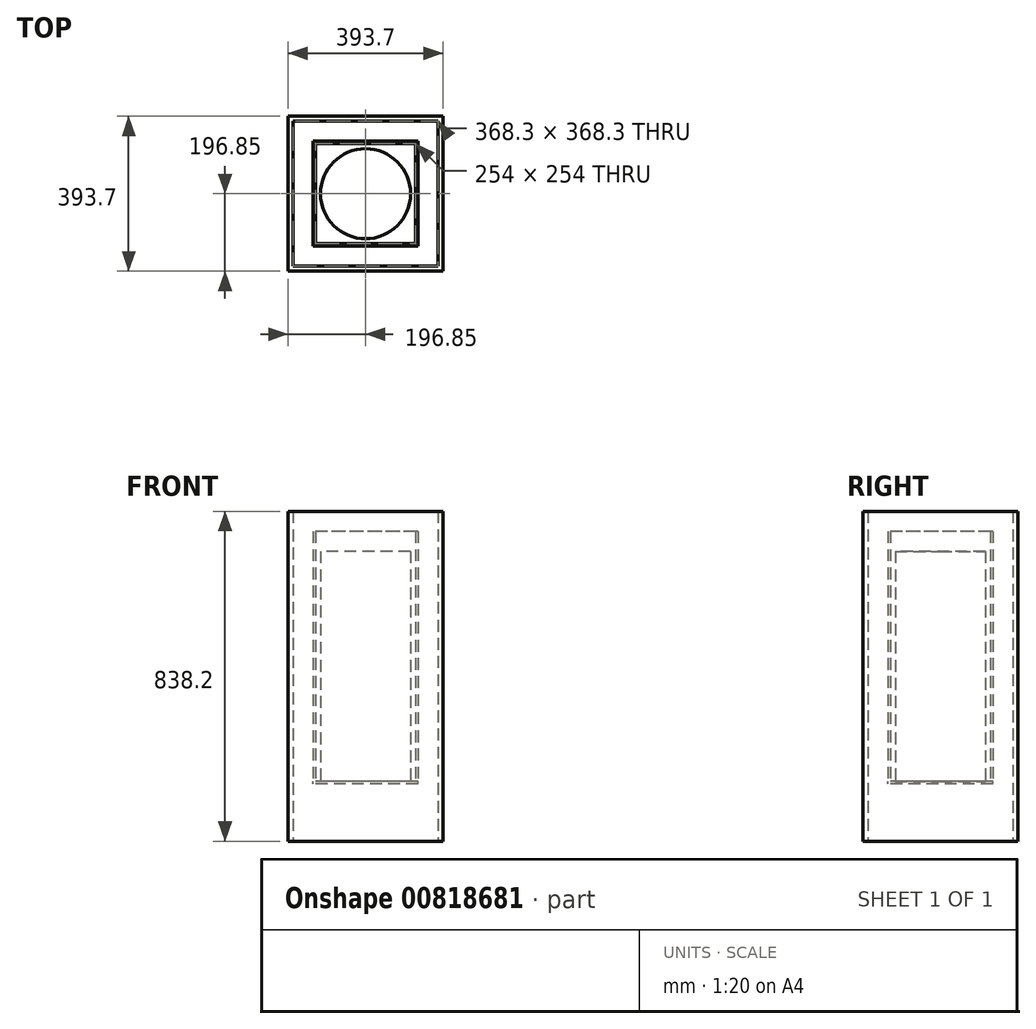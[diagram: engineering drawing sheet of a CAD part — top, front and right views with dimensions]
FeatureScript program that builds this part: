
annotation { "Feature Type Name" : "Feature", "Feature Type Description" : "" }
export const myFeature = defineFeature(function(context is Context, id is Id, definition is map)
    precondition{}
    {
        {
            var Q0;
            Q0=qCreatedBy(makeId("Top.planeOp"),FACE);
            var sketch = newSketch(context, id + "F0", { "sketchPlane" : qUnion([Q0])});
            skCircle(sketch, "E0", {"center": v(0, 0) * mm, "radius": 114.3 * mm});
            skLineSegment(sketch, "E1.bottom", {"start": v(127, 127) * mm, "end": v(-127, 127) * mm});
            skLineSegment(sketch, "E1.top", {"start": v(127, -127) * mm, "end": v(-127, -127) * mm});
            skLineSegment(sketch, "E1.left", {"start": v(127, 127) * mm, "end": v(127, -127) * mm});
            skLineSegment(sketch, "E1.right", {"start": v(-127, 127) * mm, "end": v(-127, -127) * mm});
            skLineSegment(sketch, "E2.0", {"start": v(133.35, 133.35) * mm, "end": v(-133.35, 133.35) * mm});
            skLineSegment(sketch, "E2.1", {"start": v(133.35, 133.35) * mm, "end": v(133.35, -133.35) * mm});
            skLineSegment(sketch, "E2.2", {"start": v(133.35, -133.35) * mm, "end": v(-133.35, -133.35) * mm});
            skLineSegment(sketch, "E2.3", {"start": v(-133.35, 133.35) * mm, "end": v(-133.35, -133.35) * mm});
            skLineSegment(sketch, "E3.0", {"start": v(184.15, 184.15) * mm, "end": v(-184.15, 184.15) * mm});
            skLineSegment(sketch, "E3.1", {"start": v(184.15, 184.15) * mm, "end": v(184.15, -184.15) * mm});
            skLineSegment(sketch, "E3.2", {"start": v(184.15, -184.15) * mm, "end": v(-184.15, -184.15) * mm});
            skLineSegment(sketch, "E3.3", {"start": v(-184.15, 184.15) * mm, "end": v(-184.15, -184.15) * mm});
            skLineSegment(sketch, "E4.0", {"start": v(196.85, 196.85) * mm, "end": v(-196.85, 196.85) * mm});
            skLineSegment(sketch, "E4.1", {"start": v(196.85, 196.85) * mm, "end": v(196.85, -196.85) * mm});
            skLineSegment(sketch, "E4.2", {"start": v(196.85, -196.85) * mm, "end": v(-196.85, -196.85) * mm});
            skLineSegment(sketch, "E4.3", {"start": v(-196.85, 196.85) * mm, "end": v(-196.85, -196.85) * mm});
            skSolve(sketch);
        }
        {
            var Q0;
            Q0=makeQuery(id+"F0.imprint","IMPRINT",FACE,{"disambiguationData":[TD([[makeQuery(id+"F0.imprint","IMPRINT",EDGE,{"derivedFrom":sQuery(id+"F0.wireOp",EDGE,"E0")}),1.0]])]});
            extrude(context, id + "F1", {"entities" : qUnion([Q0]), "depth" : 584.2 * mm, "offsetDistance" : 25.4 * mm});
        }
        {
            var Q0;
            Q0=makeQuery(id+"F0.imprint","IMPRINT",FACE,{"disambiguationData":[TD([[makeQuery(id+"F0.imprint","IMPRINT",EDGE,{"derivedFrom":sQuery(id+"F0.wireOp",EDGE,"E1.bottom")}),-1.0]])]});
            extrude(context, id + "F2", {"entities" : qUnion([Q0]), "depth" : 635 * mm, "offsetDistance" : 25.4 * mm});
        }
        {
            var Q0;
            Q0=makeQuery(id+"F0.imprint","IMPRINT",FACE,{"disambiguationData":[TD([[makeQuery(id+"F0.imprint","IMPRINT",EDGE,{"derivedFrom":sQuery(id+"F0.wireOp",EDGE,"E1.bottom")}),-1.0]])]});
            var Q1;
            Q1=makeQuery(id+"F0.imprint","IMPRINT",FACE,{"disambiguationData":[TD([[makeQuery(id+"F0.imprint","IMPRINT",EDGE,{"derivedFrom":sQuery(id+"F0.wireOp",EDGE,"E0")}),-1.0]])]});
            var Q2;
            Q2=makeQuery(id+"F0.imprint","IMPRINT",FACE,{"disambiguationData":[TD([[makeQuery(id+"F0.imprint","IMPRINT",EDGE,{"derivedFrom":sQuery(id+"F0.wireOp",EDGE,"E0")}),1.0]])]});
            extrude(context, id + "F3", {"entities" : qUnion([Q0, Q1, Q2]), "oppositeDirection" : true, "depth" : 6.35 * mm, "offsetDistance" : 25.4 * mm});
        }
        {
            var Q0;
            Q0=makeQuery(id+"F0.imprint","IMPRINT",FACE,{"disambiguationData":[TD([[makeQuery(id+"F0.imprint","IMPRINT",EDGE,{"derivedFrom":sQuery(id+"F0.wireOp",EDGE,"E3.0")}),-1.0]])]});
            extrude(context, id + "F4", {"entities" : qUnion([Q0]), "depth" : 685.8 * mm, "offsetDistance" : 25.4 * mm, "hasSecondDirection" : true, "secondDirectionOppositeDirection" : true, "secondDirectionDepth" : 152.4 * mm});
        }
    });
